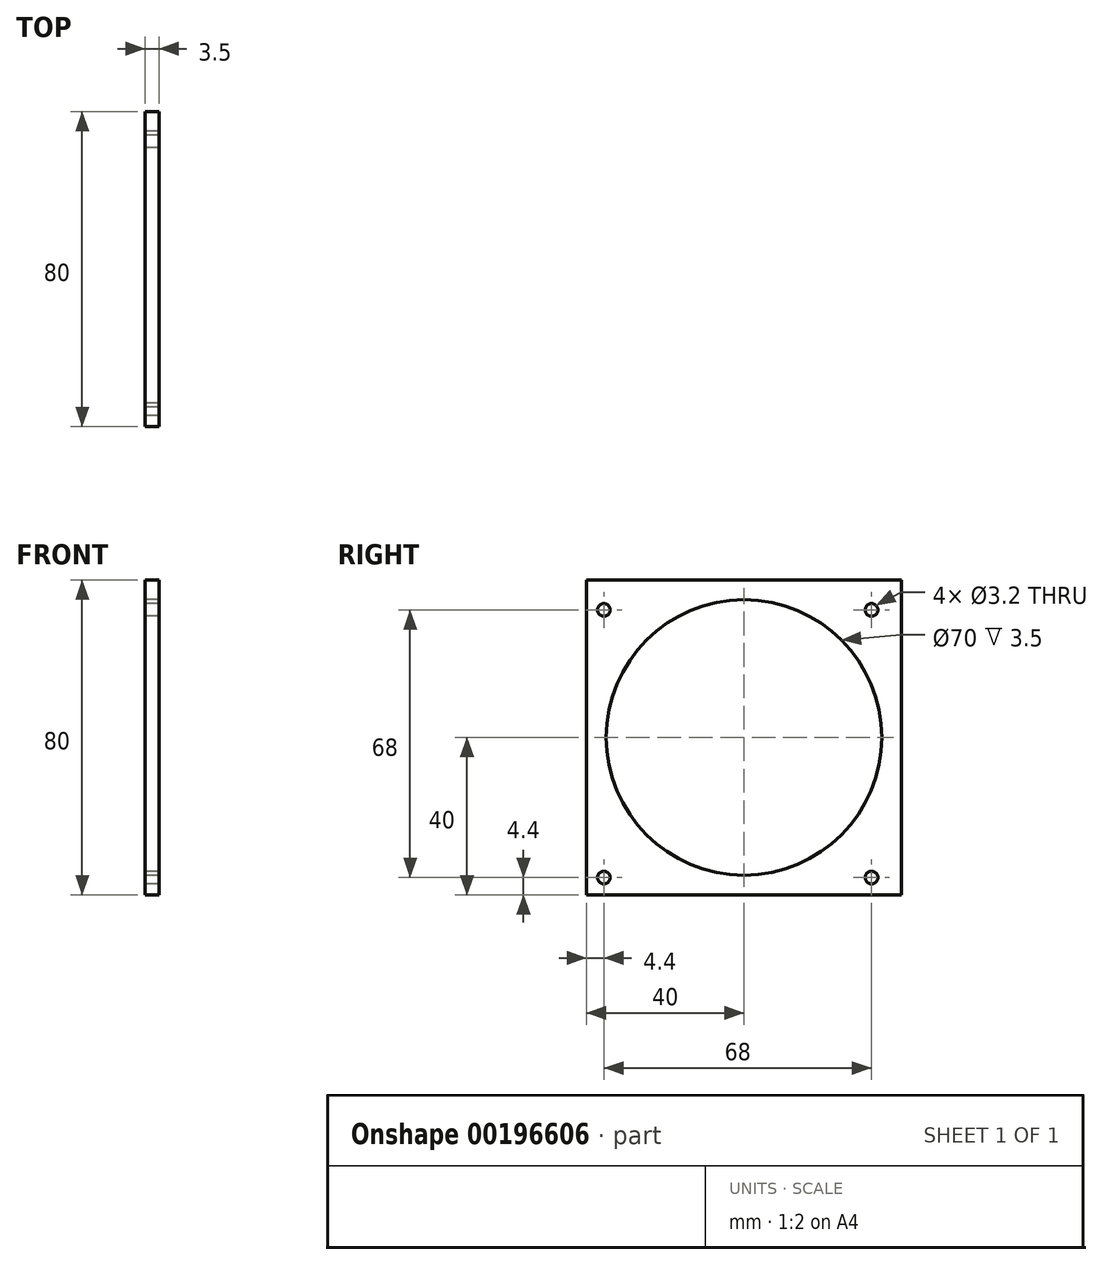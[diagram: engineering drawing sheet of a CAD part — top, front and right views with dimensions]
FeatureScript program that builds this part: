
annotation { "Feature Type Name" : "Feature", "Feature Type Description" : "" }
export const myFeature = defineFeature(function(context is Context, id is Id, definition is map)
    precondition{}
    {
        {
            var Q0;
            Q0=qCreatedBy(makeId("Right.planeOp"),FACE);
            var sketch = newSketch(context, id + "F0", { "sketchPlane" : qUnion([Q0])});
            skCircle(sketch, "E0", {"center": v(0, 0) * mm, "radius": 35 * mm});
            skLineSegment(sketch, "E1.bottom", {"start": v(-40, -40) * mm, "end": v(40, -40) * mm});
            skLineSegment(sketch, "E1.top", {"start": v(-40, 40) * mm, "end": v(40, 40) * mm});
            skLineSegment(sketch, "E1.left", {"start": v(-40, -40) * mm, "end": v(-40, 40) * mm});
            skLineSegment(sketch, "E1.right", {"start": v(40, -40) * mm, "end": v(40, 40) * mm});
            skCircle(sketch, "E2", {"center": v(32.4, 32.4) * mm, "radius": 1.6 * mm});
            skCircle(sketch, "E3.0.1.0", {"center": v(32.4, -35.6) * mm, "radius": 1.6 * mm});
            skCircle(sketch, "E3.1.0.0", {"center": v(-35.6, 32.4) * mm, "radius": 1.6 * mm});
            skCircle(sketch, "E3.1.1.0", {"center": v(-35.6, -35.6) * mm, "radius": 1.6 * mm});
            skLineSegment(sketch, "E3.direction1", {"start": v(32.4, 32.4) * mm, "end": v(-35.6, 32.4) * mm, "construction": true});
            skLineSegment(sketch, "E3.direction2", {"start": v(32.4, 32.4) * mm, "end": v(32.4, -35.6) * mm, "construction": true});
            skSolve(sketch);
        }
        {
            var Q0;
            Q0=makeQuery(id+"F0.imprint","IMPRINT",FACE,{"disambiguationData":[TD([[makeQuery(id+"F0.imprint","IMPRINT",EDGE,{"derivedFrom":sQuery(id+"F0.wireOp",EDGE,"E0")}),-1.0]])]});
            extrude(context, id + "F1", {"entities" : qUnion([Q0]), "depth" : 3.5 * mm});
        }
    });
